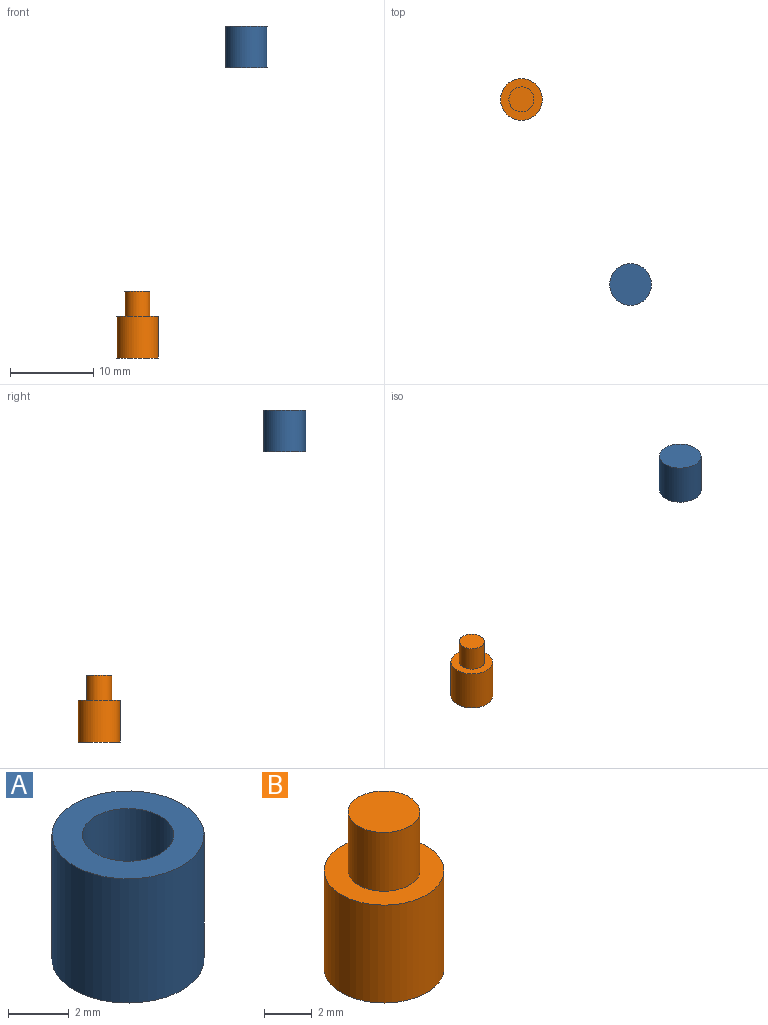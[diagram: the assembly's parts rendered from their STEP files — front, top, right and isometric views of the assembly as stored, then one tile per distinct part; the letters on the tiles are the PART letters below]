
ASSEMBLY  parts=2 mates=1
PART A: 5 faces, bbox 5x5x5 mm
  f0: plane 5x5mm, normal (0,0,1), area 12.6mm2, adj f1,f3
  f1: cylinder r=2.5mm len=5mm, axis (0,0,1), area 78.5mm2, adj f0,f2
  f2: plane 5x5mm, normal (0,0,-1), area 19.6mm2, adj f1
  f3: cylinder r=1.5mm len=4mm, axis (0,0,1), area 37.7mm2, adj f0,f4
  f4: plane 3x3mm, normal (0,0,1), area 7.1mm2, adj f3
PART B: 5 faces, bbox 5x5x8 mm
  f0: plane 5x5mm, normal (0,0,1), area 12.6mm2, adj f1,f3
  f1: cylinder r=2.5mm len=5mm, axis (0,0,1), area 78.5mm2, adj f0,f2
  f2: plane 5x5mm, normal (0,0,-1), area 19.6mm2, adj f1
  f3: cylinder r=1.5mm len=3mm, axis (0,0,-1), area 28.3mm2, adj f0,f4
  f4: plane 3x3mm, normal (0,0,1), area 7.1mm2, adj f3
PLACE A rot(axis=(0,1,0),180deg) t=(43.6,27.48,42.79)mm
PLACE B t=(30.52,49.72,7.99)mm
MATE parallel B.f1 <-> A.f1  axis (0,0,1) through (30.52,49.72,13.49)mm
